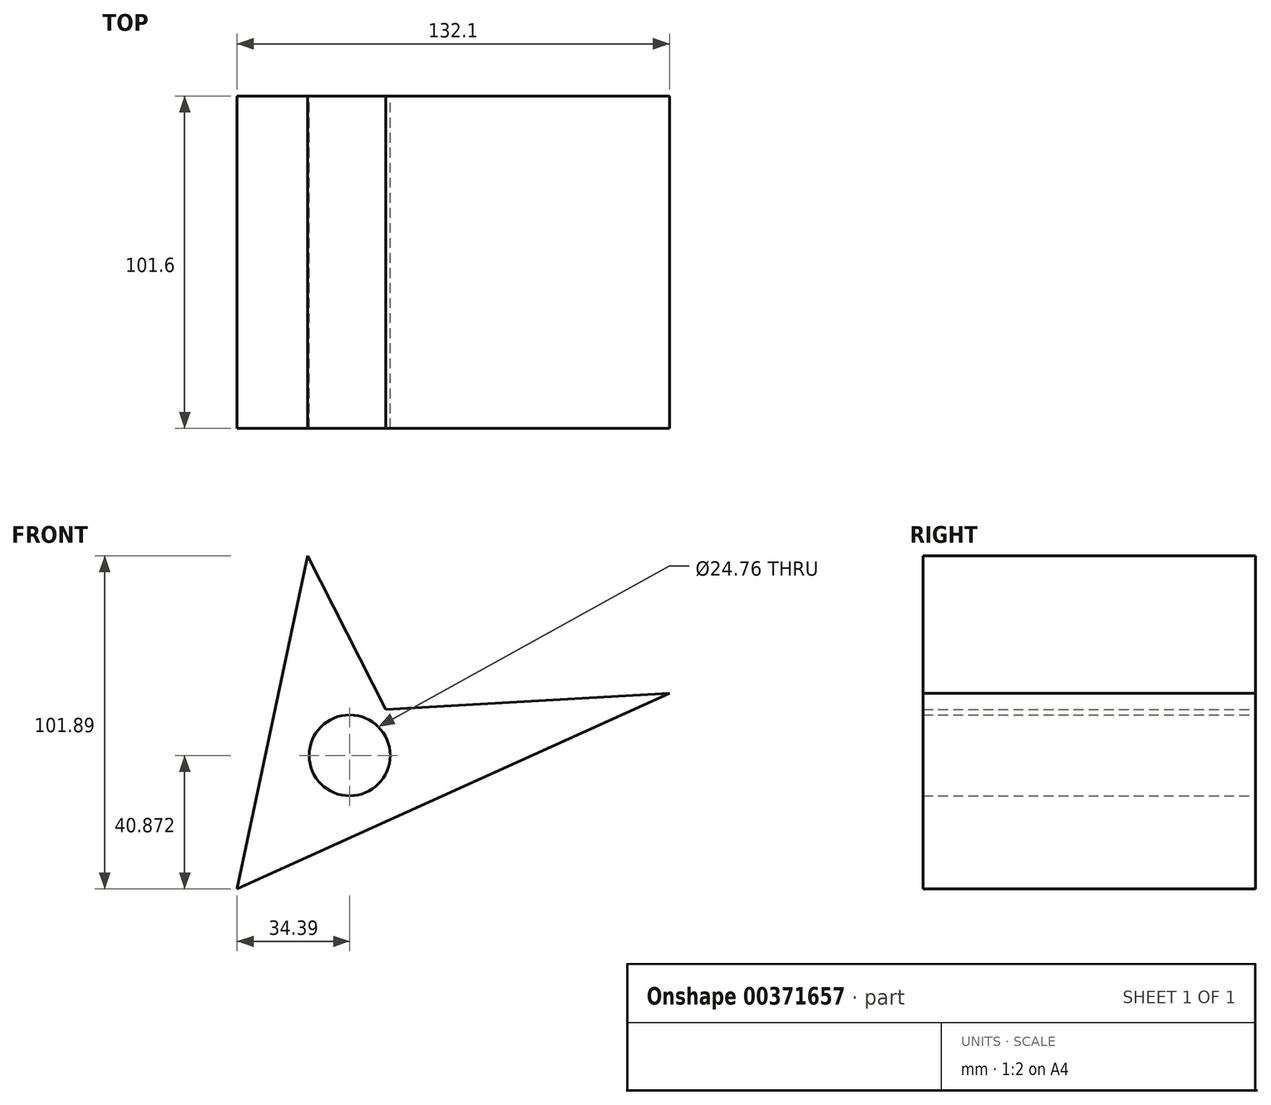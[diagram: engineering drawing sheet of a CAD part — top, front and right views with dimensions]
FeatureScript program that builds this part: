
annotation { "Feature Type Name" : "Feature", "Feature Type Description" : "" }
export const myFeature = defineFeature(function(context is Context, id is Id, definition is map)
    precondition{}
    {
        {
            var Q0;
            Q0=qCreatedBy(makeId("Front.planeOp"),FACE);
            var sketch = newSketch(context, id + "F0", { "sketchPlane" : qUnion([Q0])});
            skLineSegment(sketch, "E0", {"start": v(-42.3, 51.52) * mm, "end": v(-63.9, -50.37) * mm});
            skLineSegment(sketch, "E1", {"start": v(-63.9, -50.37) * mm, "end": v(68.2, 9.5) * mm});
            skLineSegment(sketch, "E2", {"start": v(68.2, 9.5) * mm, "end": v(-18.42, 4.6) * mm});
            skLineSegment(sketch, "E3", {"start": v(-18.42, 4.6) * mm, "end": v(-42.3, 51.52) * mm});
            skSolve(sketch);
        }
        {
            var Q0;
            Q0=makeQuery(id+"F0.imprint","IMPRINT",FACE,{"disambiguationData":[TD([[makeQuery(id+"F0.imprint","IMPRINT",EDGE,{"derivedFrom":sQuery(id+"F0.wireOp",EDGE,"E0")}),1.0]])]});
            extrude(context, id + "F1", {"entities" : qUnion([Q0]), "depth" : 101.6 * mm});
        }
        {
            var Q0;
            Q0=makeQuery(id+"F1.opExtrude","CAP_FACE",FACE,{"disambiguationData":[OSD([sQuery(id+"F0.wireOp",EDGE,"E0"),sQuery(id+"F0.wireOp",EDGE,"E1"),sQuery(id+"F0.wireOp",EDGE,"E2"),sQuery(id+"F0.wireOp",EDGE,"E3")])],"isStart":true});
            var sketch = newSketch(context, id + "F2", { "sketchPlane" : qUnion([Q0])});
            skCircle(sketch, "E4", {"center": v(29.21, -10.07) * mm, "radius": 11.75 * mm});
            skSolve(sketch);
        }
        {
            var Q0;
            Q0=makeQuery(id+"F2.imprint","IMPRINT",FACE,{"disambiguationData":[TD([[makeQuery(id+"F2.imprint","IMPRINT",EDGE,{"derivedFrom":sQuery(id+"F2.wireOp",EDGE,"E4")}),1.0]])]});
            extrude(context, id + "F3", {"entities" : qUnion([Q0]), "operationType" : NewBodyOperationType.ADD, "oppositeDirection" : true, "depth" : 101.6 * mm});
        }
        {
            var Q0;
            Q0=makeQuery(id+"F1.opExtrude","CAP_FACE",FACE,{"disambiguationData":[OSD([sQuery(id+"F0.wireOp",EDGE,"E0"),sQuery(id+"F0.wireOp",EDGE,"E1"),sQuery(id+"F0.wireOp",EDGE,"E2"),sQuery(id+"F0.wireOp",EDGE,"E3")])],"isStart":true});
            var sketch = newSketch(context, id + "F4", { "sketchPlane" : qUnion([Q0])});
            skCircle(sketch, "E5", {"center": v(29.5, -9.5) * mm, "radius": 12.38 * mm});
            skSolve(sketch);
        }
        {
            var Q0;
            Q0=makeQuery(id+"F4.imprint","IMPRINT",FACE,{"disambiguationData":[TD([[makeQuery(id+"F4.imprint","IMPRINT",EDGE,{"derivedFrom":sQuery(id+"F4.wireOp",EDGE,"E5")}),1.0]])]});
            extrude(context, id + "F5", {"entities" : qUnion([Q0]), "operationType" : NewBodyOperationType.REMOVE, "oppositeDirection" : true, "depth" : 101.6 * mm});
        }
    });
